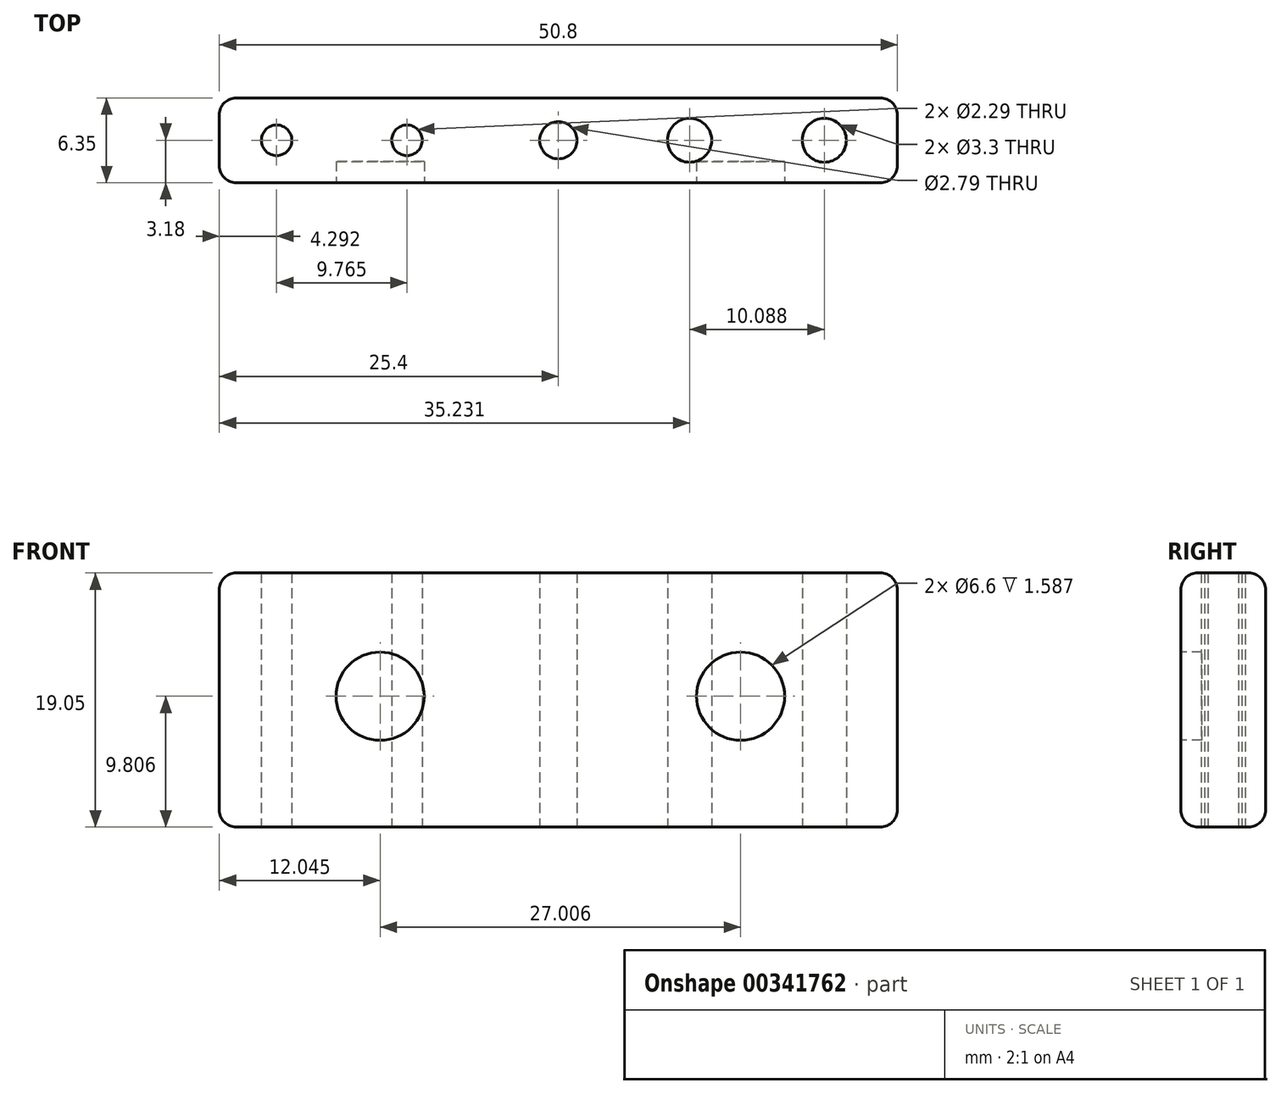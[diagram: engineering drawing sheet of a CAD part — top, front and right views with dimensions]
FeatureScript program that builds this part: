
annotation { "Feature Type Name" : "Feature", "Feature Type Description" : "" }
export const myFeature = defineFeature(function(context is Context, id is Id, definition is map)
    precondition{}
    {
        {
            var Q0;
            Q0=qCreatedBy(makeId("Top.planeOp"),FACE);
            var sketch = newSketch(context, id + "F0", { "sketchPlane" : qUnion([Q0])});
            skLineSegment(sketch, "E0.bottom", {"start": v(25.4, -3.17) * mm, "end": v(-25.4, -3.18) * mm});
            skLineSegment(sketch, "E0.top", {"start": v(25.4, 3.18) * mm, "end": v(-25.4, 3.17) * mm});
            skLineSegment(sketch, "E0.left", {"start": v(25.4, -3.17) * mm, "end": v(25.4, 3.18) * mm});
            skLineSegment(sketch, "E0.right", {"start": v(-25.4, -3.18) * mm, "end": v(-25.4, 3.17) * mm});
            skPoint(sketch, "E0.middle", {"position": v(0, 0) * mm});
            skCircle(sketch, "E1", {"center": v(-21.1, 0) * mm, "radius": 1.14 * mm});
            skCircle(sketch, "E2", {"center": v(-11.34, 0) * mm, "radius": 1.14 * mm});
            skCircle(sketch, "E3", {"center": v(0, 0) * mm, "radius": 1.4 * mm});
            skCircle(sketch, "E4", {"center": v(9.83, 0) * mm, "radius": 1.65 * mm});
            skCircle(sketch, "E5", {"center": v(19.92, 0) * mm, "radius": 1.65 * mm});
            skSolve(sketch);
        }
        {
            var Q0;
            Q0 = qSketchRegion(id + "F0", true);
            extrude(context, id + "F1", {"entities" : qUnion([Q0]), "depth" : 19.05 * mm});
        }
        {
            var Q0;
            Q0=makeQuery(id+"F1.opExtrude","CAP_EDGE",EDGE,{"disambiguationData":[OSD([sQuery(id+"F0.wireOp",EDGE,"E0.bottom")])],"isStart":false});
            var Q1;
            Q1=makeQuery(id+"F1.opExtrude","CAP_EDGE",EDGE,{"disambiguationData":[OSD([sQuery(id+"F0.wireOp",EDGE,"E0.top")])],"isStart":false});
            var Q2;
            Q2=makeQuery(id+"F1.opExtrude","CAP_EDGE",EDGE,{"disambiguationData":[OSD([sQuery(id+"F0.wireOp",EDGE,"E0.right")])],"isStart":false});
            var Q3;
            Q3=makeQuery(id+"F1.opExtrude","CAP_EDGE",EDGE,{"disambiguationData":[OSD([sQuery(id+"F0.wireOp",EDGE,"E0.left")])],"isStart":false});
            var Q4;
            Q4=makeQuery(id+"F1.opExtrude","SWEPT_EDGE",EDGE,{"disambiguationData":[OSD([sQuery(id+"F0.wireOp",EDGE,"E0.bottom"),sQuery(id+"F0.wireOp",EDGE,"E0.right")])]});
            var Q5;
            Q5=makeQuery(id+"F1.opExtrude","SWEPT_EDGE",EDGE,{"disambiguationData":[OSD([sQuery(id+"F0.wireOp",EDGE,"E0.top"),sQuery(id+"F0.wireOp",EDGE,"E0.right")])]});
            var Q6;
            Q6=makeQuery(id+"F1.opExtrude","SWEPT_EDGE",EDGE,{"disambiguationData":[OSD([sQuery(id+"F0.wireOp",EDGE,"E0.bottom"),sQuery(id+"F0.wireOp",EDGE,"E0.left")])]});
            var Q7;
            Q7=makeQuery(id+"F1.opExtrude","SWEPT_EDGE",EDGE,{"disambiguationData":[OSD([sQuery(id+"F0.wireOp",EDGE,"E0.top"),sQuery(id+"F0.wireOp",EDGE,"E0.left")])]});
            var Q8;
            Q8=makeQuery(id+"F1.opExtrude","CAP_EDGE",EDGE,{"disambiguationData":[OSD([sQuery(id+"F0.wireOp",EDGE,"E0.bottom")])],"isStart":true});
            var Q9;
            Q9=makeQuery(id+"F1.opExtrude","CAP_EDGE",EDGE,{"disambiguationData":[OSD([sQuery(id+"F0.wireOp",EDGE,"E0.top")])],"isStart":true});
            var Q10;
            Q10=makeQuery(id+"F1.opExtrude","CAP_EDGE",EDGE,{"disambiguationData":[OSD([sQuery(id+"F0.wireOp",EDGE,"E0.left")])],"isStart":true});
            var Q11;
            Q11=makeQuery(id+"F1.opExtrude","CAP_EDGE",EDGE,{"disambiguationData":[OSD([sQuery(id+"F0.wireOp",EDGE,"E0.right")])],"isStart":true});
            fillet(context, id + "F2", {"entities" : qUnion([Q0, Q1, Q2, Q3, Q4, Q5, Q6, Q7, Q8, Q9, Q10, Q11]), "radius" : 1.27 * mm, "tangentPropagation" : true, "allowEdgeOverflow" : false});
        }
        {
            var Q0;
            Q0=makeQuery(id+"F1.opExtrude","SWEPT_FACE",FACE,{"disambiguationData":[OSD([sQuery(id+"F0.wireOp",EDGE,"E0.bottom")])]});
            cPlane(context, id + "F3", {"entities" : qUnion([Q0]), "cplaneType" : CPlaneType.OFFSET, "offset" : 0 * mm, "width" : 152.4 * mm, "height" : 152.4 * mm});
        }
        {
            var Q0;
            Q0=qCreatedBy(id+"F3.planeOp",FACE);
            var sketch = newSketch(context, id + "F4", { "sketchPlane" : qUnion([Q0])});
            skCircle(sketch, "E6", {"center": v(13.65, 9.8) * mm, "radius": 3.3 * mm});
            skCircle(sketch, "E7", {"center": v(-13.35, 9.8) * mm, "radius": 3.3 * mm});
            skSolve(sketch);
        }
        {
            var Q0;
            Q0=makeQuery(id+"F4.imprint","IMPRINT",FACE,{"disambiguationData":[TD([[makeQuery(id+"F4.imprint","IMPRINT",EDGE,{"derivedFrom":sQuery(id+"F4.wireOp",EDGE,"E6")}),1.0]])]});
            var Q1;
            Q1=makeQuery(id+"F4.imprint","IMPRINT",FACE,{"disambiguationData":[TD([[makeQuery(id+"F4.imprint","IMPRINT",EDGE,{"derivedFrom":sQuery(id+"F4.wireOp",EDGE,"E7")}),1.0]])]});
            extrude(context, id + "F5", {"entities" : qUnion([Q0, Q1]), "operationType" : NewBodyOperationType.REMOVE, "oppositeDirection" : true, "depth" : 1.59 * mm});
        }
    });
